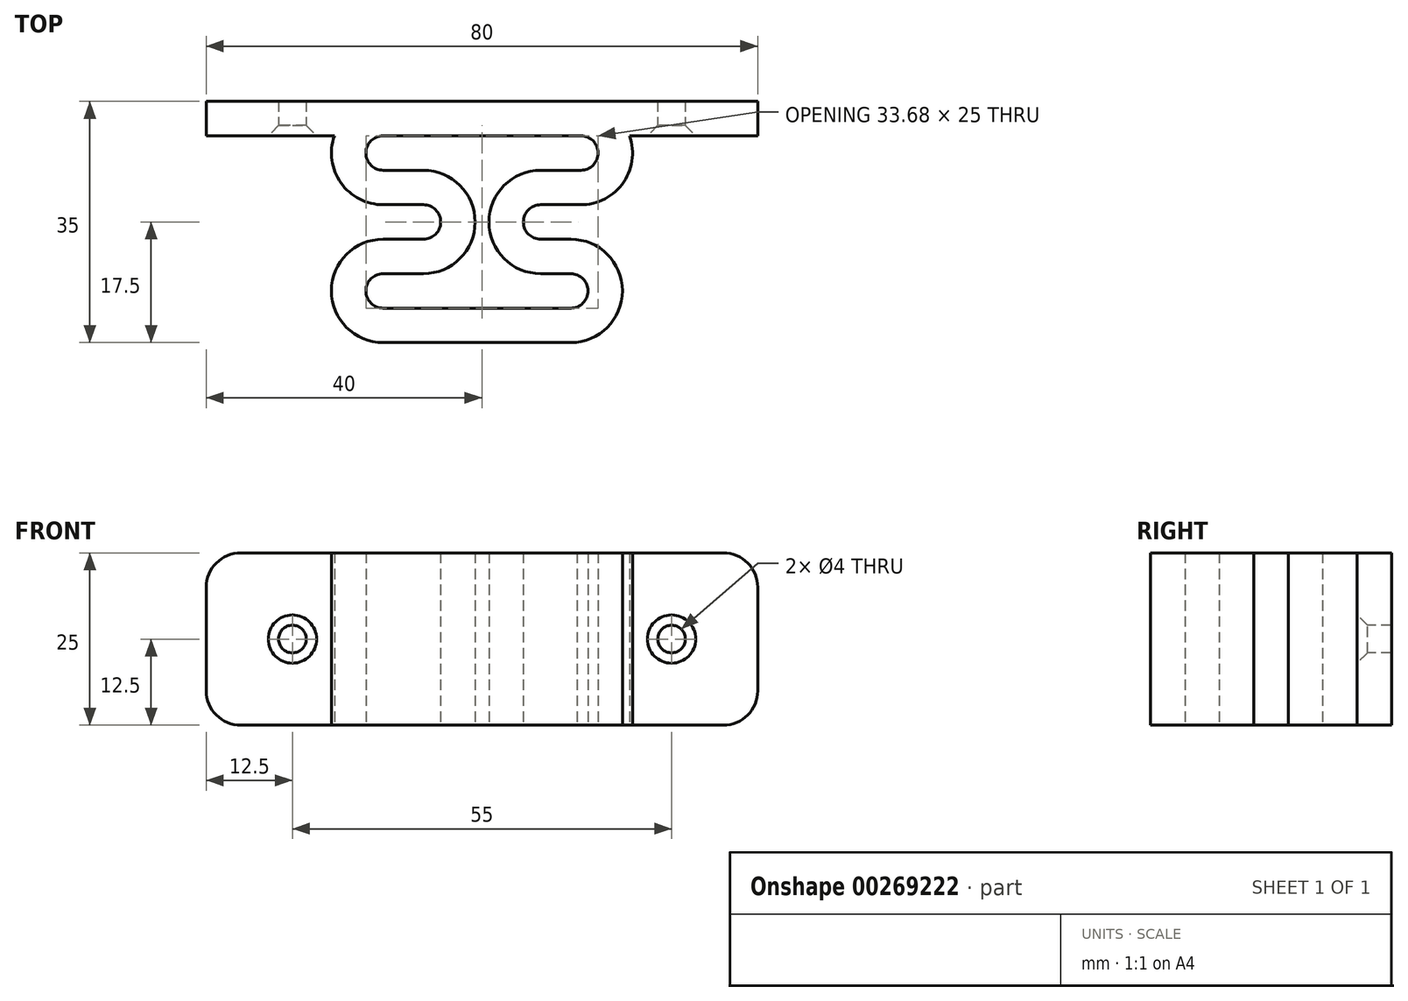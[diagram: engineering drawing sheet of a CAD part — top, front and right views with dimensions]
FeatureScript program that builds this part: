
annotation { "Feature Type Name" : "Feature", "Feature Type Description" : "" }
export const myFeature = defineFeature(function(context is Context, id is Id, definition is map)
    precondition{}
    {
        {
            var Q0;
            Q0=qCreatedBy(makeId("Top.planeOp"),FACE);
            var sketch = newSketch(context, id + "F0", { "sketchPlane" : qUnion([Q0])});
            skCircle(sketch, "E0", {"center": v(-14.34, 10) * mm, "radius": 2.5 * mm});
            skCircle(sketch, "E1", {"center": v(-14.34, 10) * mm, "radius": 7.5 * mm});
            skCircle(sketch, "E2", {"center": v(14.34, 10) * mm, "radius": 7.5 * mm});
            skCircle(sketch, "E3", {"center": v(14.34, 10) * mm, "radius": 2.5 * mm});
            skLineSegment(sketch, "E4", {"start": v(-14.34, 17.5) * mm, "end": v(14.34, 17.5) * mm});
            skPoint(sketch, "E5", {"position": v(0, 17.5) * mm});
            skLineSegment(sketch, "E6", {"start": v(-14.34, 12.5) * mm, "end": v(14.34, 12.5) * mm});
            skCircle(sketch, "E7", {"center": v(-14.34, -10) * mm, "radius": 2.5 * mm});
            skCircle(sketch, "E8", {"center": v(-14.34, -10) * mm, "radius": 7.5 * mm});
            skCircle(sketch, "E9", {"center": v(12.87, -10) * mm, "radius": 2.5 * mm});
            skCircle(sketch, "E10", {"center": v(12.87, -10) * mm, "radius": 7.5 * mm});
            skLineSegment(sketch, "E11", {"start": v(-14.34, -17.5) * mm, "end": v(12.87, -17.5) * mm});
            skLineSegment(sketch, "E12", {"start": v(-14.34, -12.5) * mm, "end": v(12.87, -12.5) * mm});
            skCircle(sketch, "E13", {"center": v(-8.5, 0) * mm, "radius": 2.5 * mm});
            skCircle(sketch, "E14", {"center": v(8.5, 0) * mm, "radius": 2.5 * mm});
            skCircle(sketch, "E15", {"center": v(-8.5, 0) * mm, "radius": 7.5 * mm});
            skCircle(sketch, "E16", {"center": v(8.5, 0) * mm, "radius": 7.5 * mm});
            skLineSegment(sketch, "E17", {"start": v(-14.34, 7.5) * mm, "end": v(-8.5, 7.5) * mm});
            skLineSegment(sketch, "E18", {"start": v(14.34, 7.5) * mm, "end": v(8.5, 7.5) * mm});
            skLineSegment(sketch, "E19", {"start": v(-8.5, 2.5) * mm, "end": v(-14.34, 2.5) * mm});
            skLineSegment(sketch, "E20", {"start": v(8.5, 2.5) * mm, "end": v(13.8, 2.52) * mm});
            skLineSegment(sketch, "E21", {"start": v(-8.5, -2.5) * mm, "end": v(-14.34, -2.5) * mm});
            skLineSegment(sketch, "E22", {"start": v(8.5, -2.5) * mm, "end": v(12.87, -2.5) * mm});
            skLineSegment(sketch, "E23", {"start": v(-14.34, -7.5) * mm, "end": v(-8.5, -7.5) * mm});
            skLineSegment(sketch, "E24", {"start": v(8.5, -7.5) * mm, "end": v(12.87, -7.5) * mm});
            skSolve(sketch);
        }
        {
            var Q0;
            {var subQ0=sQuery(id+"F0.wireOp",EDGE,"E4");Q0=makeQuery(id+"F0.imprint","IMPRINT",FACE,{"disambiguationData":[TD([[makeQuery(id+"F0.imprint","IMPRINT",EDGE,{"derivedFrom":subQ0}),-1.0]])]});}
            var Q1;
            {var subQ0=sQuery(id+"F0.wireOp",EDGE,"E1");var subQ2=sQuery(id+"F0.wireOp",EDGE,"8CR9bk30-KQ4b-ltya-m7mn-kqcPntCiqzbD");var subQ3=makeQuery(id+"F0.imprint","INTERSECT",VERTEX,{"disambiguationData":[OD(0.0)],"derivedFrom":[subQ2,subQ0]});Q1=makeQuery(id+"F0.imprint","IMPRINT",FACE,{"disambiguationData":[TD([[makeQuery(id+"F0.imprint","IMPRINT",EDGE,{"disambiguationData":[TD([[subQ3,1.0]])],"derivedFrom":subQ2}),-1.0]])]});}
            var Q2;
            {var subQ0=sQuery(id+"F0.wireOp",EDGE,"8CR9bk30-KQ4b-ltya-m7mn-kqcPntCiqzbD");var subQ1=makeQuery(id+"F0.imprint","INTERSECT",VERTEX,{"derivedFrom":[subQ0,sQuery(id+"F0.wireOp",EDGE,"E0")]});Q2=makeQuery(id+"F0.imprint","IMPRINT",FACE,{"disambiguationData":[TD([[makeQuery(id+"F0.imprint","IMPRINT",EDGE,{"disambiguationData":[TD([[subQ1,1.0]])],"derivedFrom":subQ0}),1.0]])]});}
            var Q3;
            {var subQ0=sQuery(id+"F0.wireOp",EDGE,"E1");var subQ1=sQuery(id+"F0.wireOp",EDGE,"6h7cOsYY-HjXx-50Em-QmnM-c8Dnv7Tza03D");var subQ2=makeQuery(id+"F0.imprint","INTERSECT",VERTEX,{"derivedFrom":[subQ1,subQ0]});Q3=makeQuery(id+"F0.imprint","IMPRINT",FACE,{"disambiguationData":[TD([[makeQuery(id+"F0.imprint","IMPRINT",EDGE,{"disambiguationData":[TD([[subQ2,1.0]])],"derivedFrom":subQ1}),-1.0]])]});}
            var Q4;
            {var subQ0=sQuery(id+"F0.wireOp",EDGE,"E8");var subQ1=sQuery(id+"F0.wireOp",EDGE,"8CR9bk30-KQ4b-ltya-m7mn-kqcPntCiqzbD");var subQ2=makeQuery(id+"F0.imprint","INTERSECT",VERTEX,{"disambiguationData":[OD(0.0)],"derivedFrom":[subQ1,subQ0]});Q4=makeQuery(id+"F0.imprint","IMPRINT",FACE,{"disambiguationData":[TD([[makeQuery(id+"F0.imprint","IMPRINT",EDGE,{"disambiguationData":[TD([[subQ2,-1.0]])],"derivedFrom":subQ1}),1.0]])]});}
            var Q5;
            {var subQ0=sQuery(id+"F0.wireOp",EDGE,"E8");var subQ4=sQuery(id+"F0.wireOp",EDGE,"8CR9bk30-KQ4b-ltya-m7mn-kqcPntCiqzbD");var subQ5=makeQuery(id+"F0.imprint","INTERSECT",VERTEX,{"disambiguationData":[OD(0.0)],"derivedFrom":[subQ4,subQ0]});Q5=makeQuery(id+"F0.imprint","IMPRINT",FACE,{"disambiguationData":[TD([[makeQuery(id+"F0.imprint","IMPRINT",EDGE,{"disambiguationData":[TD([[subQ5,-1.0]])],"derivedFrom":subQ4}),-1.0]])]});}
            var Q6;
            {var subQ0=sQuery(id+"F0.wireOp",EDGE,"E11");Q6=makeQuery(id+"F0.imprint","IMPRINT",FACE,{"disambiguationData":[TD([[makeQuery(id+"F0.imprint","IMPRINT",EDGE,{"derivedFrom":subQ0}),1.0]])]});}
            var Q7;
            {var subQ0=sQuery(id+"F0.wireOp",EDGE,"E10");var subQ2=sQuery(id+"F0.wireOp",EDGE,"DIOqt0p8-QBxR-8iWn-KdwK-cJBDFyHMyHgb");var subQ3=makeQuery(id+"F0.imprint","INTERSECT",VERTEX,{"disambiguationData":[OD(0.0)],"derivedFrom":[subQ2,subQ0]});Q7=makeQuery(id+"F0.imprint","IMPRINT",FACE,{"disambiguationData":[TD([[makeQuery(id+"F0.imprint","IMPRINT",EDGE,{"disambiguationData":[TD([[subQ3,1.0]])],"derivedFrom":subQ2}),-1.0]])]});}
            var Q8;
            {var subQ0=sQuery(id+"F0.wireOp",EDGE,"E10");var subQ1=sQuery(id+"F0.wireOp",EDGE,"DIOqt0p8-QBxR-8iWn-KdwK-cJBDFyHMyHgb");var subQ2=makeQuery(id+"F0.imprint","INTERSECT",VERTEX,{"disambiguationData":[OD(1.0)],"derivedFrom":[subQ1,subQ0]});Q8=makeQuery(id+"F0.imprint","IMPRINT",FACE,{"disambiguationData":[TD([[makeQuery(id+"F0.imprint","IMPRINT",EDGE,{"disambiguationData":[TD([[subQ2,-1.0]])],"derivedFrom":subQ1}),1.0]])]});}
            var Q9;
            {var subQ0=sQuery(id+"F0.wireOp",EDGE,"DIOqt0p8-QBxR-8iWn-KdwK-cJBDFyHMyHgb");var subQ1=sQuery(id+"F0.wireOp",EDGE,"E2");var subQ2=makeQuery(id+"F0.imprint","INTERSECT",VERTEX,{"disambiguationData":[OD(1.0)],"derivedFrom":[subQ1,subQ0]});Q9=makeQuery(id+"F0.imprint","IMPRINT",FACE,{"disambiguationData":[TD([[makeQuery(id+"F0.imprint","IMPRINT",EDGE,{"disambiguationData":[TD([[subQ2,-1.0]])],"derivedFrom":subQ1}),-1.0]])]});}
            var Q10;
            {var subQ1=sQuery(id+"F0.wireOp",EDGE,"E2");var subQ7=makeQuery(id+"F0.imprint","INTERSECT",VERTEX,{"derivedFrom":[subQ1,sQuery(id+"F0.wireOp",EDGE,"E4")]});Q10=makeQuery(id+"F0.imprint","IMPRINT",FACE,{"disambiguationData":[TD([[makeQuery(id+"F0.imprint","IMPRINT",EDGE,{"disambiguationData":[TD([[subQ7,-1.0]])],"derivedFrom":subQ1}),1.0]])]});}
            var Q11;
            {var subQ0=sQuery(id+"F0.wireOp",EDGE,"DIOqt0p8-QBxR-8iWn-KdwK-cJBDFyHMyHgb");var subQ1=sQuery(id+"F0.wireOp",EDGE,"E2");var subQ2=makeQuery(id+"F0.imprint","INTERSECT",VERTEX,{"disambiguationData":[OD(1.0)],"derivedFrom":[subQ1,subQ0]});Q11=makeQuery(id+"F0.imprint","IMPRINT",FACE,{"disambiguationData":[TD([[makeQuery(id+"F0.imprint","IMPRINT",EDGE,{"disambiguationData":[TD([[subQ2,-1.0]])],"derivedFrom":subQ1}),1.0]])]});}
            var Q12;
            {var subQ8=sQuery(id+"F0.wireOp",EDGE,"E17");Q12=makeQuery(id+"F0.imprint","IMPRINT",FACE,{"disambiguationData":[TD([[makeQuery(id+"F0.imprint","IMPRINT",EDGE,{"derivedFrom":subQ8}),-1.0]])]});}
            var Q13;
            {var subQ0=sQuery(id+"F0.wireOp",EDGE,"E1");var subQ1=makeQuery(id+"F0.imprint","INTERSECT",VERTEX,{"derivedFrom":[subQ0,sQuery(id+"F0.wireOp",EDGE,"E19")]});Q13=makeQuery(id+"F0.imprint","IMPRINT",FACE,{"disambiguationData":[TD([[makeQuery(id+"F0.imprint","IMPRINT",EDGE,{"disambiguationData":[TD([[subQ1,1.0]])],"derivedFrom":subQ0}),1.0]])]});}
            var Q14;
            {var subQ5=sQuery(id+"F0.wireOp",EDGE,"E19");Q14=makeQuery(id+"F0.imprint","IMPRINT",FACE,{"disambiguationData":[TD([[makeQuery(id+"F0.imprint","IMPRINT",EDGE,{"derivedFrom":subQ5}),-1.0]])]});}
            var Q15;
            {var subQ0=sQuery(id+"F0.wireOp",EDGE,"E8");var subQ1=makeQuery(id+"F0.imprint","INTERSECT",VERTEX,{"derivedFrom":[subQ0,sQuery(id+"F0.wireOp",EDGE,"E21")]});Q15=makeQuery(id+"F0.imprint","IMPRINT",FACE,{"disambiguationData":[TD([[makeQuery(id+"F0.imprint","IMPRINT",EDGE,{"disambiguationData":[TD([[subQ1,1.0]])],"derivedFrom":subQ0}),1.0]])]});}
            var Q16;
            {var subQ0=sQuery(id+"F0.wireOp",EDGE,"E10");var subQ1=makeQuery(id+"F0.imprint","INTERSECT",VERTEX,{"derivedFrom":[subQ0,sQuery(id+"F0.wireOp",EDGE,"E22")]});Q16=makeQuery(id+"F0.imprint","IMPRINT",FACE,{"disambiguationData":[TD([[makeQuery(id+"F0.imprint","IMPRINT",EDGE,{"disambiguationData":[TD([[subQ1,1.0]])],"derivedFrom":subQ0}),1.0]])]});}
            var Q17;
            {var subQ0=sQuery(id+"F0.wireOp",EDGE,"E2");var subQ1=makeQuery(id+"F0.imprint","INTERSECT",VERTEX,{"derivedFrom":[subQ0,sQuery(id+"F0.wireOp",EDGE,"E20")]});Q17=makeQuery(id+"F0.imprint","IMPRINT",FACE,{"disambiguationData":[TD([[makeQuery(id+"F0.imprint","IMPRINT",EDGE,{"disambiguationData":[TD([[subQ1,1.0]])],"derivedFrom":subQ0}),1.0]])]});}
            var Q18;
            {var subQ5=sQuery(id+"F0.wireOp",EDGE,"E20");Q18=makeQuery(id+"F0.imprint","IMPRINT",FACE,{"disambiguationData":[TD([[makeQuery(id+"F0.imprint","IMPRINT",EDGE,{"derivedFrom":subQ5}),1.0]])]});}
            var Q19;
            {var subQ8=sQuery(id+"F0.wireOp",EDGE,"E23");Q19=makeQuery(id+"F0.imprint","IMPRINT",FACE,{"disambiguationData":[TD([[makeQuery(id+"F0.imprint","IMPRINT",EDGE,{"derivedFrom":subQ8}),1.0]])]});}
            var Q20;
            {var subQ8=sQuery(id+"F0.wireOp",EDGE,"E24");Q20=makeQuery(id+"F0.imprint","IMPRINT",FACE,{"disambiguationData":[TD([[makeQuery(id+"F0.imprint","IMPRINT",EDGE,{"derivedFrom":subQ8}),1.0]])]});}
            extrude(context, id + "F1", {"entities" : qUnion([Q0, Q1, Q2, Q3, Q4, Q5, Q6, Q7, Q8, Q9, Q10, Q11, Q12, Q13, Q14, Q15, Q16, Q17, Q18, Q19, Q20]), "depth" : 25 * mm});
        }
        {
            var Q0;
            Q0=qCreatedBy(makeId("Right.planeOp"),FACE);
            var sketch = newSketch(context, id + "F2", { "sketchPlane" : qUnion([Q0])});
            skLineSegment(sketch, "E25.bottom", {"start": v(17.5, 25) * mm, "end": v(12.5, 25) * mm});
            skLineSegment(sketch, "E25.top", {"start": v(17.5, 0) * mm, "end": v(12.5, 0) * mm});
            skLineSegment(sketch, "E25.left", {"start": v(17.5, 25) * mm, "end": v(17.5, 0) * mm});
            skLineSegment(sketch, "E25.right", {"start": v(12.5, 25) * mm, "end": v(12.5, 0) * mm});
            skSolve(sketch);
        }
        {
            var Q0;
            Q0=qSketchRegion(id+"F2",true);
            extrude(context, id + "F3", {"entities" : qUnion([Q0]), "operationType" : NewBodyOperationType.ADD, "depth" : 80 * mm, "symmetric" : true});
        }
        {
            var Q0;
            Q0=makeQuery(id+"F3.opExtrude","CAP_EDGE",EDGE,{"disambiguationData":[OSD([sQuery(id+"F2.wireOp",EDGE,"E25.top")])],"isStart":false});
            var Q1;
            Q1=makeQuery(id+"F3.opExtrude","CAP_EDGE",EDGE,{"disambiguationData":[OSD([sQuery(id+"F2.wireOp",EDGE,"E25.bottom")])],"isStart":false});
            var Q2;
            Q2=makeQuery(id+"F3.opExtrude","CAP_EDGE",EDGE,{"disambiguationData":[OSD([sQuery(id+"F2.wireOp",EDGE,"E25.bottom")])],"isStart":true});
            var Q3;
            Q3=makeQuery(id+"F3.opExtrude","CAP_EDGE",EDGE,{"disambiguationData":[OSD([sQuery(id+"F2.wireOp",EDGE,"E25.top")])],"isStart":true});
            fillet(context, id + "F4", {"entities" : qUnion([Q0, Q1, Q2, Q3]), "radius" : 5 * mm, "tangentPropagation" : true, "allowEdgeOverflow" : false});
        }
        {
            var Q0;
            {var subQ0=sQuery(id+"F0.wireOp",EDGE,"E1");var subQ25=sQuery(id+"F2.wireOp",EDGE,"E25.right");Q0=makeQuery(id+"F3.boolean.opBoolean","SPLIT",FACE,{"disambiguationData":[TD([makeQuery(id+"F1.opExtrude","SWEPT_FACE",FACE,{"disambiguationData":[OSD([subQ0])]})])],"derivedFrom":makeQuery(id+"F3.opExtrude","SWEPT_FACE",FACE,{"disambiguationData":[OSD([subQ25])]})});}
            var sketch = newSketch(context, id + "F5", { "sketchPlane" : qUnion([Q0])});
            skPoint(sketch, "E26", {"position": v(-27.5, 12.5) * mm});
            skPoint(sketch, "E27", {"position": v(27.5, 12.5) * mm});
            skPoint(sketch, "E28", {"position": v(-40, 12.5) * mm});
            skLineSegment(sketch, "E29", {"start": v(-40, 12.5) * mm, "end": v(-27.5, 12.5) * mm});
            skLineSegment(sketch, "E30", {"start": v(-27.5, 25) * mm, "end": v(-27.5, 12.5) * mm});
            skLineSegment(sketch, "E31", {"start": v(40, 12.5) * mm, "end": v(27.5, 12.5) * mm});
            skLineSegment(sketch, "E32", {"start": v(27.5, 12.5) * mm, "end": v(27.5, 25) * mm});
            skSolve(sketch);
        }
        {
            var Q0;
            Q0=sQuery(id+"F5.wireOp",VERTEX,"E27");
            var Q1;
            Q1=sQuery(id+"F5.wireOp",VERTEX,"E26");
            var Q2;
            Q2=makeQuery(id+"F1.opExtrude","SWEPT_BODY",BODY,{"disambiguationData":[OSD([sQuery(id+"F0.wireOp",EDGE,"E0"),sQuery(id+"F0.wireOp",EDGE,"E1"),sQuery(id+"F0.wireOp",EDGE,"E2"),sQuery(id+"F0.wireOp",EDGE,"E3"),sQuery(id+"F0.wireOp",EDGE,"E4"),sQuery(id+"F0.wireOp",EDGE,"E6"),sQuery(id+"F0.wireOp",EDGE,"E7"),sQuery(id+"F0.wireOp",EDGE,"E8"),sQuery(id+"F0.wireOp",EDGE,"E9"),sQuery(id+"F0.wireOp",EDGE,"E10"),sQuery(id+"F0.wireOp",EDGE,"E11"),sQuery(id+"F0.wireOp",EDGE,"E12"),sQuery(id+"F0.wireOp",EDGE,"E13"),sQuery(id+"F0.wireOp",EDGE,"E14"),sQuery(id+"F0.wireOp",EDGE,"E15"),sQuery(id+"F0.wireOp",EDGE,"E16"),sQuery(id+"F0.wireOp",EDGE,"E17"),sQuery(id+"F0.wireOp",EDGE,"E18"),sQuery(id+"F0.wireOp",EDGE,"E19"),sQuery(id+"F0.wireOp",EDGE,"E20"),sQuery(id+"F0.wireOp",EDGE,"E21"),sQuery(id+"F0.wireOp",EDGE,"E22"),sQuery(id+"F0.wireOp",EDGE,"E23"),sQuery(id+"F0.wireOp",EDGE,"E24")])]});
            hole(context, id + "F6", {"style" : HoleStyle.C_SINK, "endStyle" : HoleEndStyle.THROUGH, "holeDiameter" : 4 * mm, "cSinkDiameter" : 7 * mm, "cSinkAngle" : 90 * degree, "tappedDepth" : 13.2 * mm, "tapClearance" : 3, "startFromSketch" : true, "locations" : qUnion([Q0, Q1]), "scope" : qUnion([Q2])});
        }
    });
